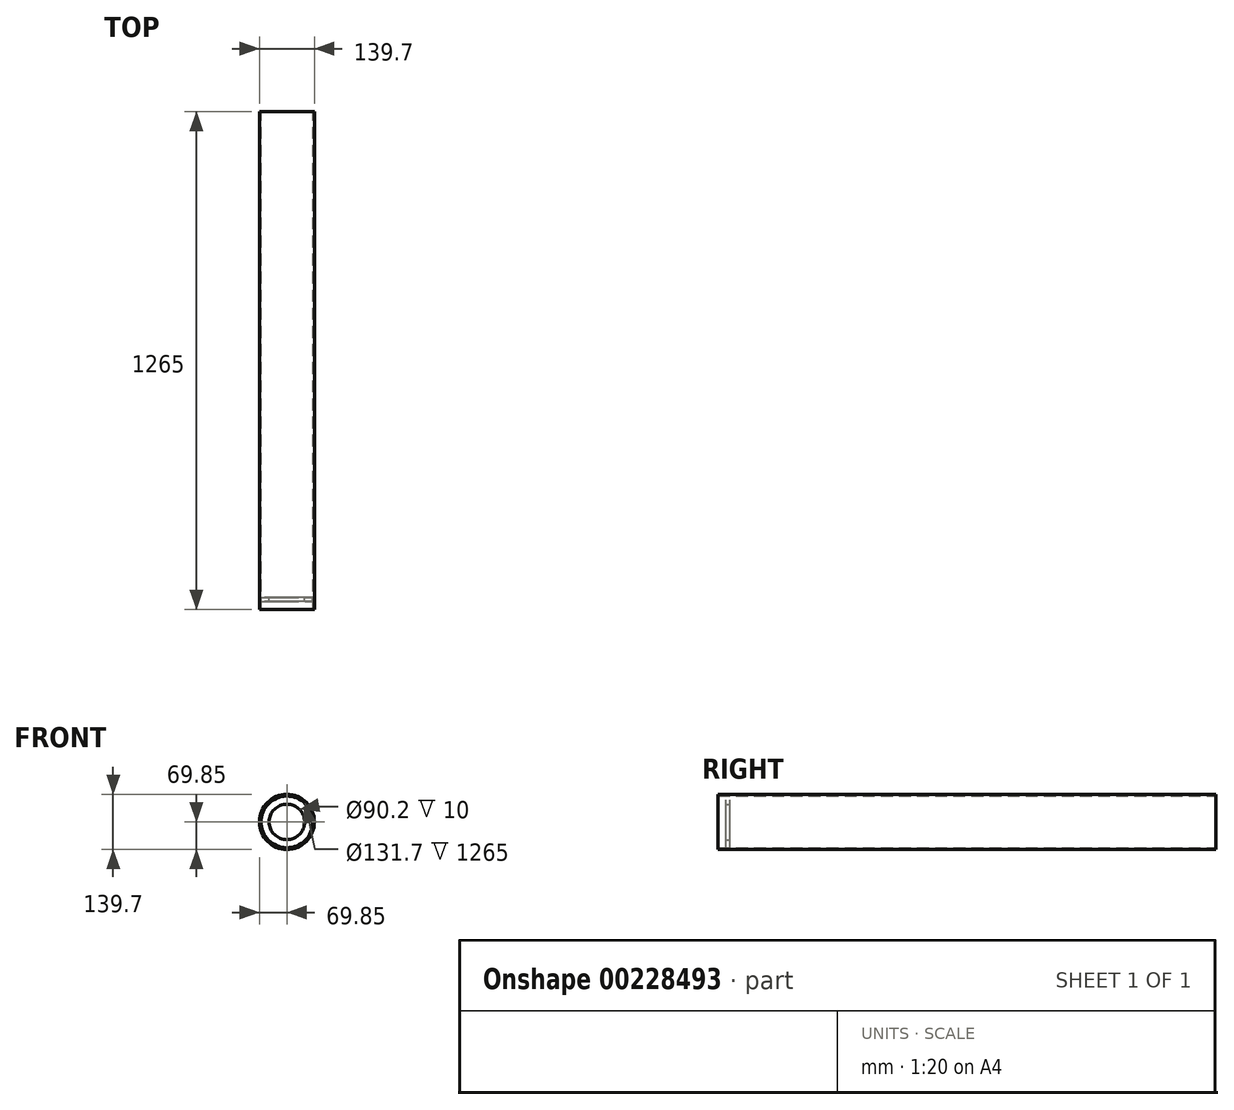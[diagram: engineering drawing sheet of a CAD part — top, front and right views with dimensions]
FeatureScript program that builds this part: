
annotation { "Feature Type Name" : "Feature", "Feature Type Description" : "" }
export const myFeature = defineFeature(function(context is Context, id is Id, definition is map)
    precondition{}
    {
        {
            assignVariable(context, id + "F0", {"name" : "L", "anyValue" : 1265});
        }
        {
            var Q0;
            Q0=qCreatedBy(makeId("Front.planeOp"),FACE);
            var sketch = newSketch(context, id + "F1", { "sketchPlane" : qUnion([Q0])});
            skCircle(sketch, "E0", {"center": v(0, 0) * mm, "radius": 45.1 * mm});
            skCircle(sketch, "E1", {"center": v(0, 0) * mm, "radius": 69.85 * mm});
            skCircle(sketch, "E2.0", {"center": v(0, 0) * mm, "radius": 65.85 * mm});
            skCircle(sketch, "E3", {"center": v(0, 0) * mm, "radius": 65.6 * mm});
            skSolve(sketch);
        }
        {
            var Q0;
            Q0=makeQuery(id+"F1.imprint","IMPRINT",FACE,{"disambiguationData":[TD([[makeQuery(id+"F1.imprint","IMPRINT",EDGE,{"derivedFrom":sQuery(id+"F1.wireOp",EDGE,"E1")}),1.0]])]});
            extrude(context, id + "F2", {"entities" : qUnion([Q0]), "depth" : (getVariable(context, 'L')) * mm, "hasSecondDirection" : true, "secondDirectionOppositeDirection" : true, "secondDirectionDepth" : 25 * mm, "symmetric" : true});
        }
        {
            var Q0;
            Q0=makeQuery(id+"F1.imprint","IMPRINT",FACE,{"disambiguationData":[TD([[makeQuery(id+"F1.imprint","IMPRINT",EDGE,{"derivedFrom":sQuery(id+"F1.wireOp",EDGE,"E0")}),-1.0]])]});
            var Q1;
            Q1=makeQuery(id+"F2.opExtrude","CAP_FACE",FACE,{"disambiguationData":[OSD([sQuery(id+"F1.wireOp",EDGE,"E1"),sQuery(id+"F1.wireOp",EDGE,"E3")])],"isStart":false});
            var Q2;
            Q2=makeQuery(id+"F2.opExtrude","CAP_FACE",FACE,{"disambiguationData":[OSD([sQuery(id+"F1.wireOp",EDGE,"E1"),sQuery(id+"F1.wireOp",EDGE,"E3")])],"isStart":false});
            extrude(context, id + "F3", {"entities" : qUnion([Q0]), "endBound" : BoundingType.UP_TO_SURFACE, "endBoundEntityFace" : qUnion([Q1]), "depth" : (getVariable(context, 'L') / 2 - 20) * mm, "hasSecondDirection" : true, "secondDirectionBound" : BoundingType.UP_TO_SURFACE, "secondDirectionOppositeDirection" : false, "secondDirectionBoundEntityFace" : qUnion([Q2]), "secondDirectionDepth" : (getVariable(context, 'L') / 2 - 25) * mm, "hasOffset" : true, "offsetDistance" : 20 * mm, "hasSecondDirectionOffset" : true, "secondDirectionOffsetDistance" : 30 * mm});
        }
    });
